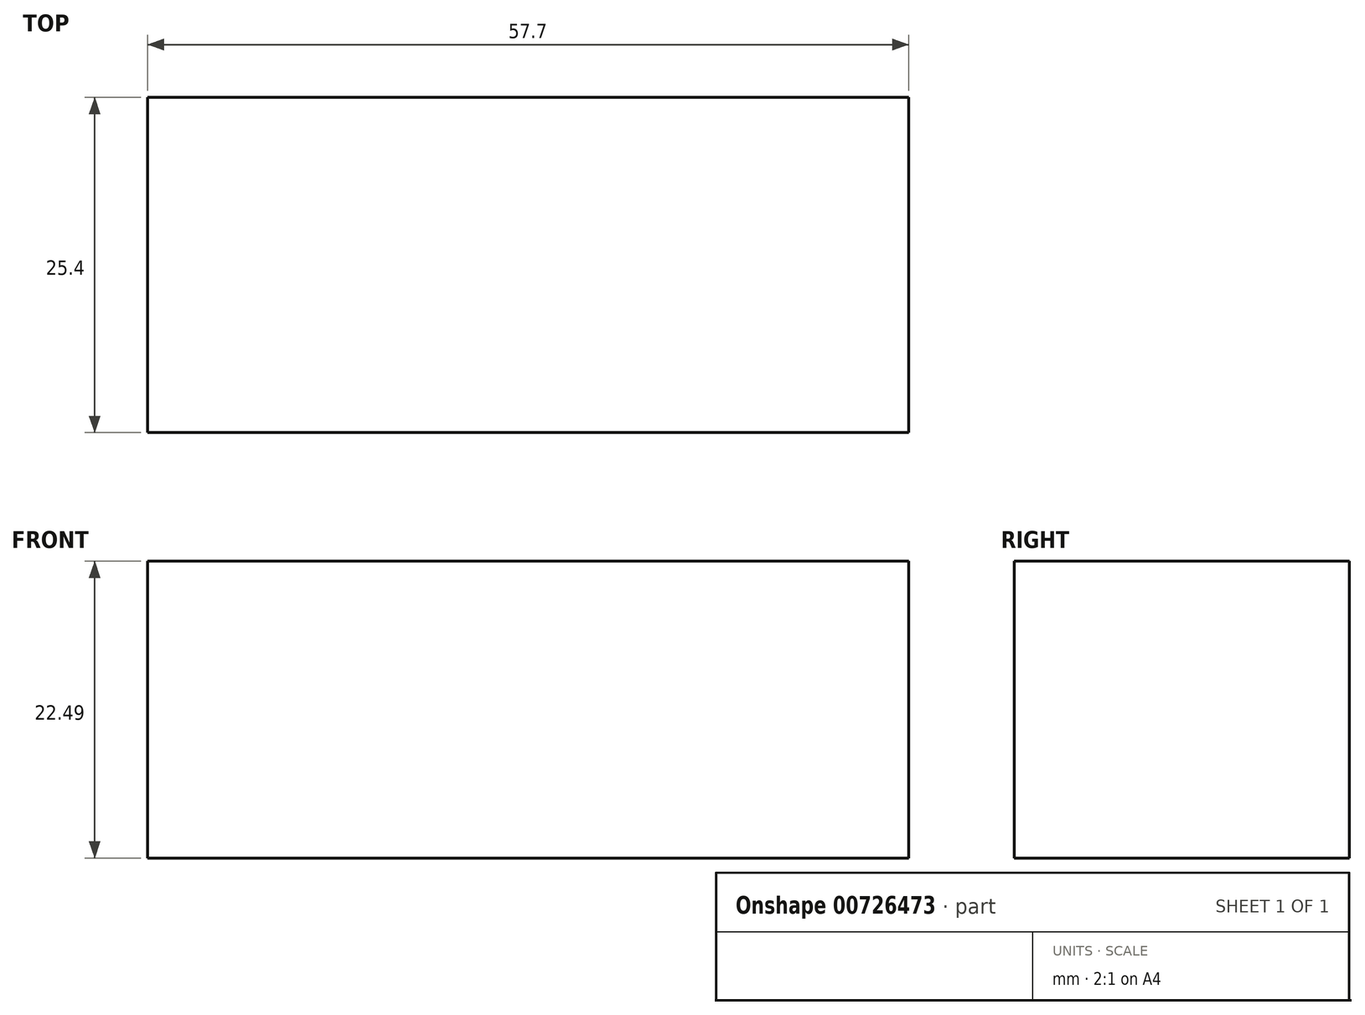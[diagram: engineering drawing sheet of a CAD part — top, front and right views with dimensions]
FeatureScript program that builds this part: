
annotation { "Feature Type Name" : "Feature", "Feature Type Description" : "" }
export const myFeature = defineFeature(function(context is Context, id is Id, definition is map)
    precondition{}
    {
        {
            var Q0;
            Q0=qCreatedBy(makeId("Front.planeOp"),FACE);
            var sketch = newSketch(context, id + "F0", { "sketchPlane" : qUnion([Q0])});
            skLineSegment(sketch, "E0.bottom", {"start": v(-70.7, 54.48) * mm, "end": v(-13, 54.48) * mm});
            skLineSegment(sketch, "E0.top", {"start": v(-70.7, 31.99) * mm, "end": v(-13, 31.99) * mm});
            skLineSegment(sketch, "E0.left", {"start": v(-70.7, 54.48) * mm, "end": v(-70.7, 31.99) * mm});
            skLineSegment(sketch, "E0.right", {"start": v(-13, 54.48) * mm, "end": v(-13, 31.99) * mm});
            skSolve(sketch);
        }
        {
            var Q0;
            Q0=makeQuery(id+"F0.imprint","IMPRINT",FACE,{"disambiguationData":[TD([[makeQuery(id+"F0.imprint","IMPRINT",EDGE,{"derivedFrom":sQuery(id+"F0.wireOp",EDGE,"E0.bottom")}),-1.0]])]});
            extrude(context, id + "F1", {"entities" : qUnion([Q0]), "depth" : 25.4 * mm, "offsetDistance" : 25.4 * mm});
        }
    });
